# Revit family: Recycle_Chute_Chutes
name_source: partatom
category: Specialty Equipment
units: mm (PartAtom-declared; Revit-internal decimal feet)

## family parameters
Always vertical = Yes
Classification Number = 23.70.30.21.21
Cut with Voids When Loaded = No
Enable Cutting in Views = No
Maintain Annotation Orientation = No
Part Type = Normal
Room Calculation Point = No
Round Connector Dimension = Use Diameter
Shared = No
Work Plane-Based = No

## types (1)
- Recycle_Chute_Chutes
    Assembly Code = D1090500
    Chute Radius = 12"
    Construction Details = http://www.arcat.com
    Default Elevation = 0"
    Description = Chute as Specified in 14 91 00
    Diameter = 24"
    Discharge Length = 30"
    Discharge Width = 24"
    Door Height = 18"
    Door Width = 21"
    Expected Lifespan (Years) = 0
    Floor Plate Size = 33"
    Green Building-LEED = http://www.arcat.com
    Installation-Fabrication = http://www.chutes.com
    Keynote = 14 91 00
    Maintenance Schedule (Months) = 0
    Manufacturer = CHUTES International
    Manufacturer Fax = 301-753-4108
    Manufacturer Website = http://www.chutes.com
    Material = Aluminized Steel - Chutes
    Model = As Specified in 14 91 00
    Product Data = http://www.arcat.com
    Product Properties = http://www.arcat.com
    Revision = R1_10-2010
    Sales Information = http://www.chutes.com
    Send Message = http://www.arcat.com
    Specification = http://www.arcat.com
    URL = http://www.chutes.com
    Warranty Duration (Years) = 0

## geometry (parser evidence)
native form markers: Blend x6, Sweep x6
no freeform markers — native parametric forms only
